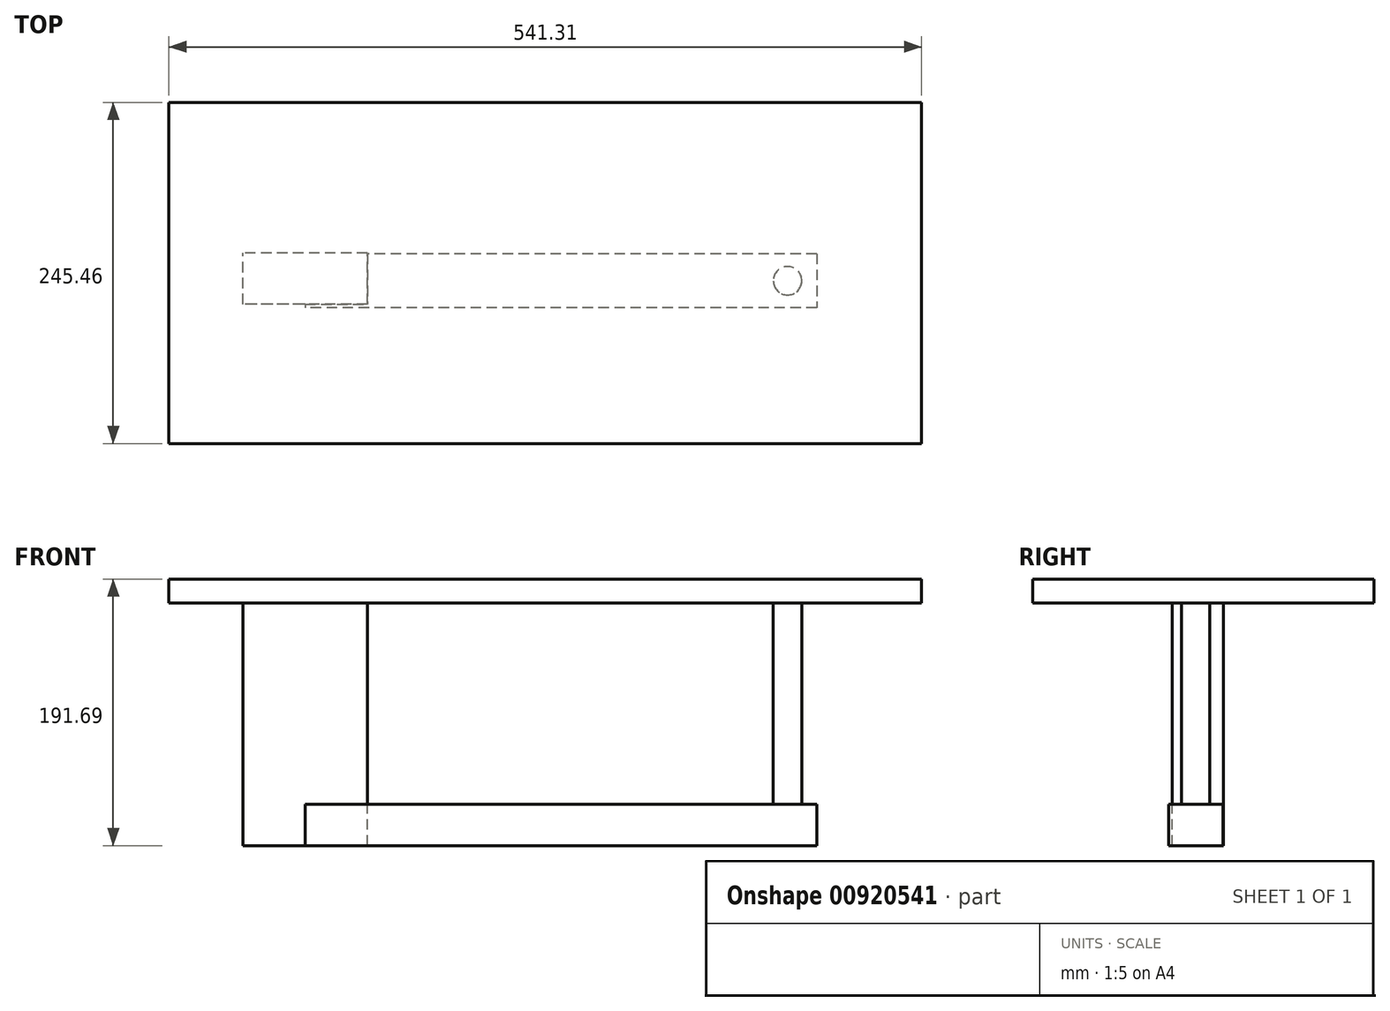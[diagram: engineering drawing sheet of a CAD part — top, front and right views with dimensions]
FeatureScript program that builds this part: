
annotation { "Feature Type Name" : "Feature", "Feature Type Description" : "" }
export const myFeature = defineFeature(function(context is Context, id is Id, definition is map)
    precondition{}
    {
        {
            var Q0;
            Q0=qCreatedBy(makeId("Top.planeOp"),FACE);
            var sketch = newSketch(context, id + "F0", { "sketchPlane" : qUnion([Q0])});
            skLineSegment(sketch, "E0.bottom", {"start": v(44.81, 0) * mm, "end": v(-44.81, 0) * mm});
            skLineSegment(sketch, "E0.top", {"start": v(44.81, 36.93) * mm, "end": v(-44.81, 36.93) * mm});
            skLineSegment(sketch, "E0.left", {"start": v(44.81, 0) * mm, "end": v(44.81, 36.93) * mm});
            skLineSegment(sketch, "E0.right", {"start": v(-44.81, 0) * mm, "end": v(-44.81, 36.93) * mm});
            skPoint(sketch, "E0.middle", {"position": v(0, 18.46) * mm});
            skSolve(sketch);
        }
        {
            var Q0;
            Q0 = qSketchRegion(id + "F0", true);
            extrude(context, id + "F1", {"entities" : qUnion([Q0]), "depth" : 174.33 * mm, "offsetDistance" : 25.4 * mm});
        }
        {
            var Q0;
            Q0=qCreatedBy(makeId("Right.planeOp"),FACE);
            var sketch = newSketch(context, id + "F2", { "sketchPlane" : qUnion([Q0])});
            skLineSegment(sketch, "E1.bottom", {"start": v(36.36, 0) * mm, "end": v(-2.6, 0) * mm});
            skLineSegment(sketch, "E1.top", {"start": v(36.36, 29.56) * mm, "end": v(-2.6, 29.56) * mm});
            skLineSegment(sketch, "E1.left", {"start": v(36.36, 0) * mm, "end": v(36.36, 29.56) * mm});
            skLineSegment(sketch, "E1.right", {"start": v(-2.6, 0) * mm, "end": v(-2.6, 29.56) * mm});
            skPoint(sketch, "E1.middle", {"position": v(16.88, 14.78) * mm});
            skSolve(sketch);
        }
        {
            var Q0;
            Q0=makeQuery(id+"F1.opExtrude","CAP_FACE",FACE,{"disambiguationData":[OSD([sQuery(id+"F0.wireOp",EDGE,"E0.bottom"),sQuery(id+"F0.wireOp",EDGE,"E0.top"),sQuery(id+"F0.wireOp",EDGE,"E0.left"),sQuery(id+"F0.wireOp",EDGE,"E0.right")])],"isStart":false});
            var sketch = newSketch(context, id + "F3", { "sketchPlane" : qUnion([Q0])});
            skLineSegment(sketch, "E2.bottom", {"start": v(-97.86, 145.25) * mm, "end": v(443.45, 145.25) * mm});
            skLineSegment(sketch, "E2.top", {"start": v(-97.86, -100.21) * mm, "end": v(443.45, -100.21) * mm});
            skLineSegment(sketch, "E2.left", {"start": v(-97.86, 145.25) * mm, "end": v(-97.86, -100.21) * mm});
            skLineSegment(sketch, "E2.right", {"start": v(443.45, 145.25) * mm, "end": v(443.45, -100.21) * mm});
            skSolve(sketch);
        }
        {
            var Q0;
            Q0 = qSketchRegion(id + "F3", true);
            extrude(context, id + "F4", {"entities" : qUnion([Q0]), "operationType" : NewBodyOperationType.ADD, "depth" : 17.36 * mm, "offsetDistance" : 25.4 * mm});
        }
        {
            var Q0;
            Q0 = qSketchRegion(id + "F2", true);
            extrude(context, id + "F5", {"entities" : qUnion([Q0]), "operationType" : NewBodyOperationType.ADD, "depth" : 368.04 * mm, "offsetDistance" : 25.4 * mm});
        }
        {
            var Q0;
            Q0=makeQuery(id+"F5.boolean.opBoolean","MERGE",FACE,{"derivedFrom":[makeQuery(id+"F1.opExtrude","CAP_FACE",FACE,{"disambiguationData":[OSD([sQuery(id+"F0.wireOp",EDGE,"E0.bottom"),sQuery(id+"F0.wireOp",EDGE,"E0.top"),sQuery(id+"F0.wireOp",EDGE,"E0.left"),sQuery(id+"F0.wireOp",EDGE,"E0.right")])],"isStart":true}),makeQuery(id+"F5.opExtrude","SWEPT_FACE",FACE,{"disambiguationData":[OSD([sQuery(id+"F2.wireOp",EDGE,"E1.bottom")])]})]});
            var sketch = newSketch(context, id + "F6", { "sketchPlane" : qUnion([Q0])});
            skCircle(sketch, "E3", {"center": v(347.03, -16.88) * mm, "radius": 10.25 * mm});
            skSolve(sketch);
        }
        {
            var Q0;
            Q0 = qSketchRegion(id + "F6", true);
            extrude(context, id + "F7", {"entities" : qUnion([Q0]), "operationType" : NewBodyOperationType.ADD, "oppositeDirection" : true, "depth" : 180.28 * mm, "offsetDistance" : 25.4 * mm});
        }
    });
